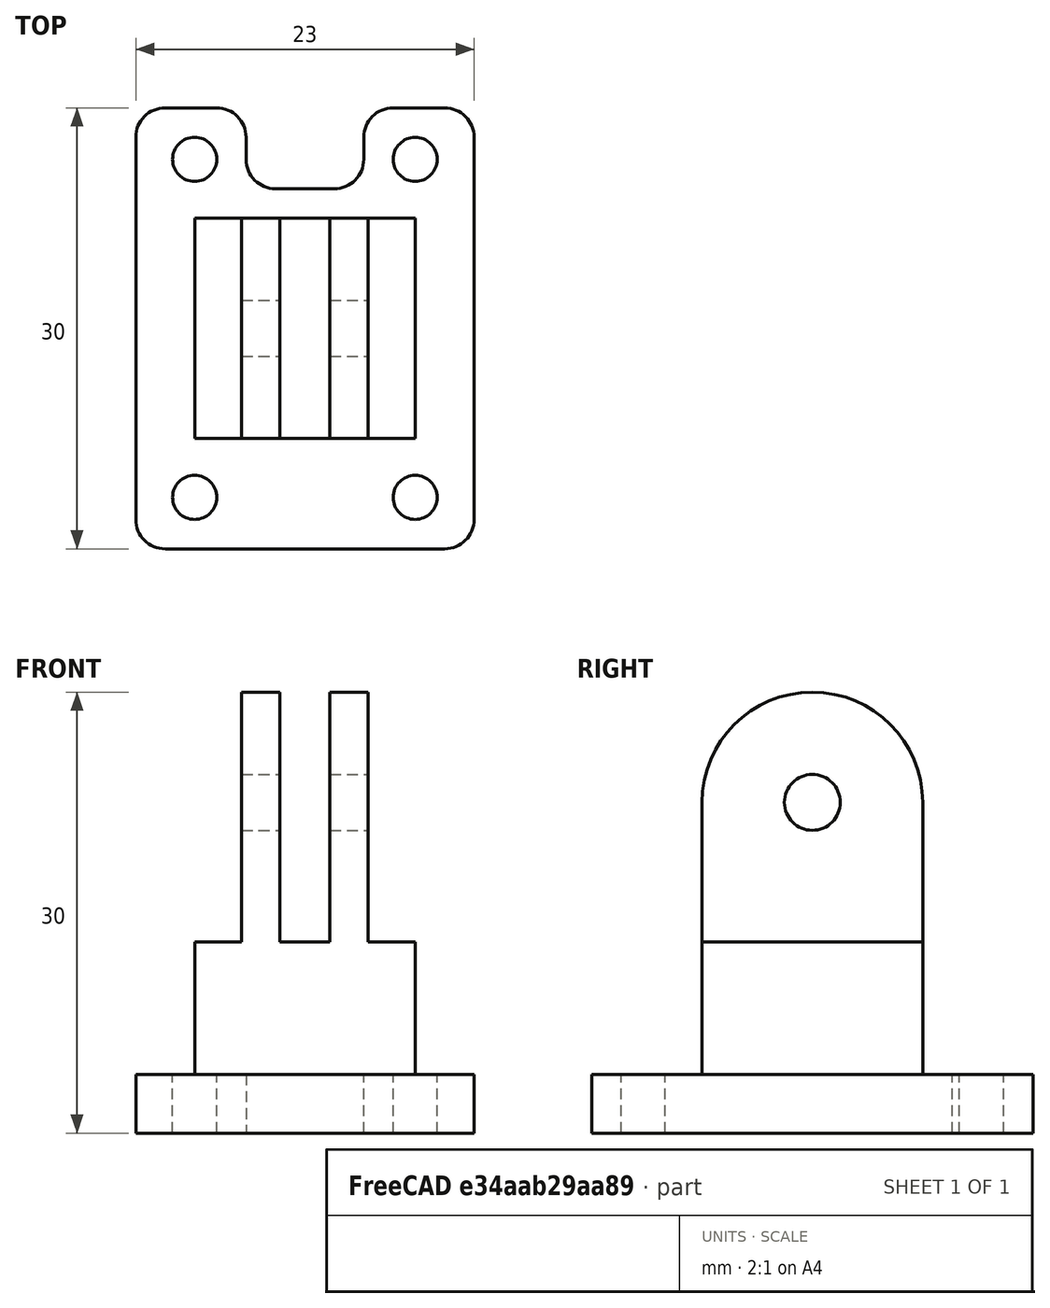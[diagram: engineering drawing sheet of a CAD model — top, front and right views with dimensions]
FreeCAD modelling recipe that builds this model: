
FCSTD DOCUMENT  (FreeCAD 0.19R23578 (Git))
Label: UV_GUVA-S12SD_sensor
License: FreeArt
LicenseURL: http://artlibre.org/licence/lal
objects: Part::Box×3, Part::MultiFuse×2, Spreadsheet::Sheet×1, Part::Cylinder×1, Part::FeaturePython×1, Part::Feature×1, Part::Cut×1, Part::Fillet×1, App::Part×1
note: 10 computed .brp shape members not serialized (recipe doc carries the construction recipe); baked Part::Feature solids carry a one-line shape summary decoded from their .brp

FEATURE [Spreadsheet::Sheet] Spreadsheet  label="p"
  cells = A1=pcb_x; B1(pcb_x)=23; A2=pcb_y; B2(pcb_y)=30; A3=pcb_z; B3(pcb_z)=1.6; A4=pcb_fwd; B4(pcb_fwd)=2; A5=pcb_back; B5(pcb_back)=2; A6=stand_x; B6(stand_x)=6; A7=stand_y; B7(stand_y)=6; A8=hole_dist_x; B8(hole_dist_x)=15; A9=hole_dist_y; B9(hole_dist_y)=23; A10=hole_r; B10(hole_r)=1.5; A11=stick_width; B11(stick_width)=15; A12=stick_length; B12(stick_length)=10; A13=pcb_wall; B13(pcb_wall)=4; A14=remove_block_x; B14(remove_block_x)=8; A15=remove_block_y; B15(remove_block_y)=6
FEATURE [Part::Cylinder] Cylinder  label="bolt hole"
  Angle = 360
  AttacherType = Attacher::AttachEngine3D
  Height = 10
  Radius = 1.5
  expr: Radius = <<p>>.hole_r
FEATURE [Part::FeaturePython] Array  label="bolt hole array"  # Draft array (typed FeaturePython)
  Angle = 360
  ArrayType = 0
  Axis = (0,0,1)
  Base = -> Cylinder
  Center = (0,0,0)
  Fuse = false
  IntervalAxis = (0,0,0)
  IntervalX = (15,0,0)
  IntervalY = (0,23,0)
  IntervalZ = (0,0,1)
  NumberPolar = 1
  NumberX = 2
  NumberY = 2
  NumberZ = 1
  Placement = pos=(0,-4,-2) rot=(0,0,1;0rad)
  expr: .Placement.Base.y = (<<p>>.stick_width - <<p>>.hole_dist_y) / 2
  expr: .Placement.Base.x = (<<p>>.stick_width - <<p>>.hole_dist_x) / 2
  expr: .IntervalY.y = <<p>>.hole_dist_y
  expr: .IntervalX.x = <<p>>.hole_dist_x
FEATURE [Part::Box] Box002  label="stick cube"
  AttacherType = Attacher::AttachEngine3D
  Height = 10
  Length = 15
  Placement = pos=(0,0,2) rot=(0,0,1;0rad)
  Width = 15
  expr: Length = <<p>>.stick_width
  expr: Width = <<p>>.stick_width
  expr: .Placement.Base.z = <<p>>.pcb_back
  expr: Height = <<p>>.stick_length
FEATURE [Part::Feature] Cut001001  label="side 2 cut001"
  Placement = pos=(7.5,7.5,12) rot=(0,0,1;1.5708rad)
  shape: bbox 15 x 15 x 20 mm, 16 faces (baked)
  expr: .Placement.Base.y = <<p>>.stick_width / 2
  expr: .Placement.Base.x = <<p>>.stick_width / 2
  expr: .Placement.Base.z = <<p>>.pcb_back + <<p>>.stick_length
FEATURE [Part::Box] Box003  label="pcb wall"
  AttacherType = Attacher::AttachEngine3D
  Height = 4
  Length = 23
  Placement = pos=(-4,-7.5,2) rot=(0,0,1;0rad)
  Width = 30
  expr: .Placement.Base.z = <<p>>.pcb_wall / 2
  expr: .Placement.Base.y = -(<<p>>.pcb_y - <<p>>.stick_width) / 2
  expr: .Placement.Base.x = -(<<p>>.pcb_x - <<p>>.stick_width) / 2
  expr: Length = <<p>>.pcb_x
  expr: Width = <<p>>.pcb_y
  expr: Height = <<p>>.pcb_wall
FEATURE [Part::MultiFuse] Fusion  label="holder fusion"
  Shapes = -> [Box002,Cut001001,Box003]
FEATURE [Part::Box] Box  label="remove block"
  AttacherType = Attacher::AttachEngine3D
  Height = 10
  Length = 8
  Placement = pos=(3.5,17,0) rot=(0,0,1;0rad)
  Width = 6
  expr: Width = <<p>>.remove_block_y
  expr: Length = <<p>>.remove_block_x
FEATURE [Part::MultiFuse] Fusion001  label="extract fusion"
  Shapes = -> [Array,Box]
FEATURE [Part::Cut] Cut  label="sensor cut"
  Base = -> Fusion
  Tool = -> Fusion001
FEATURE [Part::Fillet] Fillet  label="sensor fillet"
  Base = -> Cut
  Edges = 8 edges r=2: [Edge17,Edge19,Edge20,Edge22,Edge25,Edge26,Edge28,Edge31]
FEATURE [App::Part] Part  label="UV sensor part"
  Group = -> [Fillet]
  Origin = -> Origin
